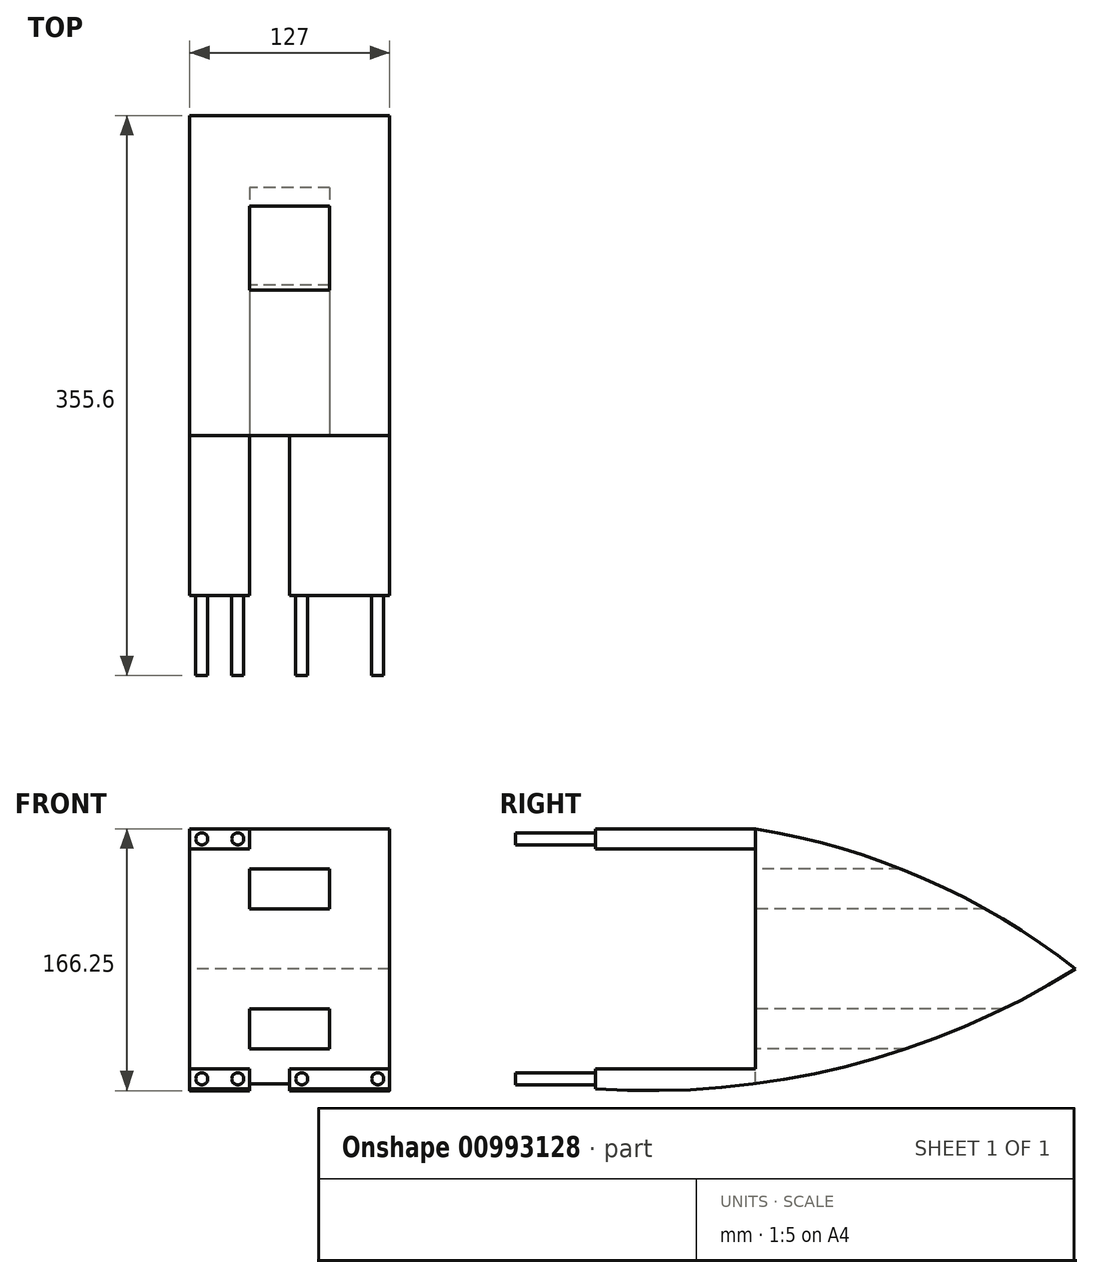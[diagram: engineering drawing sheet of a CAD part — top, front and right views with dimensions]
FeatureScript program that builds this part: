
annotation { "Feature Type Name" : "Feature", "Feature Type Description" : "" }
export const myFeature = defineFeature(function(context is Context, id is Id, definition is map)
    precondition{}
    {
        {
            var Q0;
            Q0=qCreatedBy(makeId("Right.planeOp"),FACE);
            var sketch = newSketch(context, id + "F0", { "sketchPlane" : qUnion([Q0])});
            skLineSegment(sketch, "E0", {"start": v(-50.03, 29.01) * mm, "end": v(153.17, 29.01) * mm});
            skLineSegment(sketch, "E1", {"start": v(-50.03, 29.01) * mm, "end": v(-50.03, 117.91) * mm});
            skLineSegment(sketch, "E2", {"start": v(-50.03, 29.01) * mm, "end": v(-50.03, -34.49) * mm});
            skLineSegment(sketch, "E3", {"start": v(-50.03, -34.49) * mm, "end": v(-151.63, -34.49) * mm});
            skLineSegment(sketch, "E4", {"start": v(-151.63, -34.49) * mm, "end": v(-151.63, -47.19) * mm});
            skArc(sketch, "E5", {"start": v(-151.63, -47.19) * mm, "mid": v(6.77, -33.08) * mm, "end": v(153.17, 29.01) * mm});
            skArc(sketch, "E6", {"start": v(153.17, 29.01) * mm, "mid": v(57.18, 86.27) * mm, "end": v(-50.03, 117.91) * mm});
            skSolve(sketch);
        }
        {
            var Q0;
            Q0=makeQuery(id+"F0.imprint","IMPRINT",FACE,{"disambiguationData":[TD([[makeQuery(id+"F0.imprint","IMPRINT",EDGE,{"derivedFrom":sQuery(id+"F0.wireOp",EDGE,"E0")}),1.0]])]});
            var Q1;
            Q1=makeQuery(id+"F0.imprint","IMPRINT",FACE,{"disambiguationData":[TD([[makeQuery(id+"F0.imprint","IMPRINT",EDGE,{"derivedFrom":sQuery(id+"F0.wireOp",EDGE,"E0")}),-1.0]])]});
            extrude(context, id + "F1", {"entities" : qUnion([Q0, Q1]), "depth" : 127 * mm, "offsetDistance" : 25.4 * mm});
        }
        {
            var Q0;
            Q0=makeQuery(id+"F1.opExtrude","SWEPT_FACE",FACE,{"disambiguationData":[OSD([sQuery(id+"F0.wireOp",EDGE,"E3")])]});
            var sketch = newSketch(context, id + "F2", { "sketchPlane" : qUnion([Q0])});
            skLineSegment(sketch, "E7.bottom", {"start": v(63.5, -50.03) * mm, "end": v(38.1, -50.03) * mm});
            skLineSegment(sketch, "E7.top", {"start": v(63.5, -151.63) * mm, "end": v(38.1, -151.63) * mm});
            skLineSegment(sketch, "E7.left", {"start": v(63.5, -50.03) * mm, "end": v(63.5, -151.63) * mm});
            skLineSegment(sketch, "E7.right", {"start": v(38.1, -50.03) * mm, "end": v(38.1, -151.63) * mm});
            skSolve(sketch);
        }
        {
            var Q0;
            Q0=makeQuery(id+"F2.imprint","IMPRINT",FACE,{"disambiguationData":[TD([[makeQuery(id+"F2.imprint","IMPRINT",EDGE,{"derivedFrom":sQuery(id+"F2.wireOp",EDGE,"E7.bottom")}),1.0]])]});
            extrude(context, id + "F3", {"entities" : qUnion([Q0]), "operationType" : NewBodyOperationType.REMOVE, "oppositeDirection" : true, "depth" : 25.4 * mm, "offsetDistance" : 25.4 * mm});
        }
        {
            var Q0;
            Q0=makeQuery(id+"F3.boolean.opBoolean","MERGE",FACE,{"derivedFrom":[makeQuery(id+"F1.opExtrude","SWEPT_FACE",FACE,{"disambiguationData":[OSD([sQuery(id+"F0.wireOp",EDGE,"E1"),sQuery(id+"F0.wireOp",EDGE,"E2")])]})],"fromTools":[makeQuery(id+"F3.opExtrude","SWEPT_FACE",FACE,{"disambiguationData":[OSD([sQuery(id+"F2.wireOp",EDGE,"E7.bottom")])]})]});
            var sketch = newSketch(context, id + "F4", { "sketchPlane" : qUnion([Q0])});
            skLineSegment(sketch, "E8.bottom", {"start": v(88.9, 92.51) * mm, "end": v(38.1, 92.51) * mm});
            skLineSegment(sketch, "E8.top", {"start": v(88.9, 67.11) * mm, "end": v(38.1, 67.11) * mm});
            skLineSegment(sketch, "E8.left", {"start": v(88.9, 92.51) * mm, "end": v(88.9, 67.11) * mm});
            skLineSegment(sketch, "E8.right", {"start": v(38.1, 92.51) * mm, "end": v(38.1, 67.11) * mm});
            skPoint(sketch, "E8.middle", {"position": v(63.5, 79.81) * mm});
            skPoint(sketch, "E8.middle.positionSnap0", {"position": v(63.5, 117.91) * mm});
            skPoint(sketch, "E8.centerSnap0", {"position": v(63.5, 117.91) * mm});
            skLineSegment(sketch, "E9.bottom", {"start": v(88.9, 3.61) * mm, "end": v(38.1, 3.61) * mm});
            skLineSegment(sketch, "E9.top", {"start": v(88.9, -21.79) * mm, "end": v(38.1, -21.79) * mm});
            skLineSegment(sketch, "E9.left", {"start": v(88.9, 3.61) * mm, "end": v(88.9, -21.79) * mm});
            skLineSegment(sketch, "E9.right", {"start": v(38.1, 3.61) * mm, "end": v(38.1, -21.79) * mm});
            skPoint(sketch, "E9.middle", {"position": v(63.5, -9.09) * mm});
            skSolve(sketch);
        }
        {
            var Q0;
            Q0=makeQuery(id+"F4.imprint","IMPRINT",FACE,{"disambiguationData":[TD([[makeQuery(id+"F4.imprint","IMPRINT",EDGE,{"derivedFrom":sQuery(id+"F4.wireOp",EDGE,"E8.bottom")}),1.0]])]});
            var Q1;
            Q1=makeQuery(id+"F4.imprint","IMPRINT",FACE,{"disambiguationData":[TD([[makeQuery(id+"F4.imprint","IMPRINT",EDGE,{"derivedFrom":sQuery(id+"F4.wireOp",EDGE,"E9.bottom")}),1.0]])]});
            extrude(context, id + "F5", {"entities" : qUnion([Q0, Q1]), "operationType" : NewBodyOperationType.REMOVE, "oppositeDirection" : true, "depth" : 203.2 * mm, "offsetDistance" : 25.4 * mm});
        }
        {
            var Q0;
            {var subQ1=sQuery(id+"F0.wireOp",EDGE,"E4");Q0=makeQuery(id+"F3.boolean.opBoolean","SPLIT",FACE,{"disambiguationData":[TD([makeQuery(id+"F3.opExtrude","SWEPT_FACE",FACE,{"disambiguationData":[OSD([sQuery(id+"F2.wireOp",EDGE,"E7.left")])]})])],"derivedFrom":makeQuery(id+"F1.opExtrude","SWEPT_FACE",FACE,{"disambiguationData":[OSD([subQ1])]})});}
            var sketch = newSketch(context, id + "F6", { "sketchPlane" : qUnion([Q0])});
            skCircle(sketch, "E10", {"center": v(119.38, -40.84) * mm, "radius": 3.81 * mm});
            skPoint(sketch, "E10.centerSnap0", {"position": v(127, -40.84) * mm});
            skCircle(sketch, "E11", {"center": v(71.12, -40.84) * mm, "radius": 3.81 * mm});
            skPoint(sketch, "E11.centerSnap0", {"position": v(63.5, -40.84) * mm});
            skSolve(sketch);
        }
        {
            var Q0;
            Q0=makeQuery(id+"F6.imprint","IMPRINT",FACE,{"disambiguationData":[TD([[makeQuery(id+"F6.imprint","IMPRINT",EDGE,{"derivedFrom":sQuery(id+"F6.wireOp",EDGE,"E11")}),1.0]])]});
            var Q1;
            Q1=makeQuery(id+"F6.imprint","IMPRINT",FACE,{"disambiguationData":[TD([[makeQuery(id+"F6.imprint","IMPRINT",EDGE,{"derivedFrom":sQuery(id+"F6.wireOp",EDGE,"E10")}),1.0]])]});
            extrude(context, id + "F7", {"entities" : qUnion([Q0, Q1]), "operationType" : NewBodyOperationType.ADD, "depth" : 50.8 * mm, "offsetDistance" : 25.4 * mm});
        }
        {
            var Q0;
            {var subQ1=sQuery(id+"F0.wireOp",EDGE,"E4");Q0=makeQuery(id+"F3.boolean.opBoolean","SPLIT",FACE,{"disambiguationData":[TD([makeQuery(id+"F3.opExtrude","SWEPT_FACE",FACE,{"disambiguationData":[OSD([sQuery(id+"F2.wireOp",EDGE,"E7.right")])]})])],"derivedFrom":makeQuery(id+"F1.opExtrude","SWEPT_FACE",FACE,{"disambiguationData":[OSD([subQ1])]})});}
            var sketch = newSketch(context, id + "F8", { "sketchPlane" : qUnion([Q0])});
            skCircle(sketch, "E12", {"center": v(30.48, -40.84) * mm, "radius": 3.81 * mm});
            skPoint(sketch, "E12.centerSnap0", {"position": v(38.1, -40.84) * mm});
            skCircle(sketch, "E13", {"center": v(7.62, -40.84) * mm, "radius": 3.82 * mm});
            skPoint(sketch, "E13.centerSnap0", {"position": v(0, -40.84) * mm});
            skSolve(sketch);
        }
        {
            var Q0;
            Q0=makeQuery(id+"F8.imprint","IMPRINT",FACE,{"disambiguationData":[TD([[makeQuery(id+"F8.imprint","IMPRINT",EDGE,{"derivedFrom":sQuery(id+"F8.wireOp",EDGE,"E13")}),1.0]])]});
            var Q1;
            Q1=makeQuery(id+"F8.imprint","IMPRINT",FACE,{"disambiguationData":[TD([[makeQuery(id+"F8.imprint","IMPRINT",EDGE,{"derivedFrom":sQuery(id+"F8.wireOp",EDGE,"E12")}),1.0]])]});
            extrude(context, id + "F9", {"entities" : qUnion([Q0, Q1]), "operationType" : NewBodyOperationType.ADD, "depth" : 50.8 * mm, "offsetDistance" : 25.4 * mm});
        }
        {
            var Q0;
            Q0=makeQuery(id+"F3.boolean.opBoolean","MERGE",FACE,{"derivedFrom":[makeQuery(id+"F1.opExtrude","SWEPT_FACE",FACE,{"disambiguationData":[OSD([sQuery(id+"F0.wireOp",EDGE,"E1"),sQuery(id+"F0.wireOp",EDGE,"E2")])]})],"fromTools":[makeQuery(id+"F3.opExtrude","SWEPT_FACE",FACE,{"disambiguationData":[OSD([sQuery(id+"F2.wireOp",EDGE,"E7.bottom")])]})]});
            var sketch = newSketch(context, id + "F10", { "sketchPlane" : qUnion([Q0])});
            skLineSegment(sketch, "E14.bottom", {"start": v(38.1, 105.21) * mm, "end": v(0, 105.21) * mm});
            skLineSegment(sketch, "E14.top", {"start": v(38.1, 117.91) * mm, "end": v(0, 117.91) * mm});
            skLineSegment(sketch, "E14.left", {"start": v(38.1, 105.21) * mm, "end": v(38.1, 117.91) * mm});
            skLineSegment(sketch, "E14.right", {"start": v(0, 105.21) * mm, "end": v(0, 117.91) * mm});
            skSolve(sketch);
        }
        {
            var Q0;
            Q0=makeQuery(id+"F10.imprint","IMPRINT",FACE,{"disambiguationData":[TD([[makeQuery(id+"F10.imprint","IMPRINT",EDGE,{"derivedFrom":sQuery(id+"F10.wireOp",EDGE,"E14.bottom")}),-1.0]])]});
            extrude(context, id + "F11", {"entities" : qUnion([Q0]), "operationType" : NewBodyOperationType.ADD, "depth" : 101.6 * mm, "offsetDistance" : 25.4 * mm});
        }
        {
            var Q0;
            Q0=makeQuery(id+"F11.opExtrude","CAP_FACE",FACE,{"disambiguationData":[OSD([sQuery(id+"F10.wireOp",EDGE,"E14.bottom"),sQuery(id+"F10.wireOp",EDGE,"E14.top"),sQuery(id+"F10.wireOp",EDGE,"E14.left"),sQuery(id+"F10.wireOp",EDGE,"E14.right")])],"isStart":false});
            var sketch = newSketch(context, id + "F12", { "sketchPlane" : qUnion([Q0])});
            skCircle(sketch, "E15", {"center": v(30.48, 111.56) * mm, "radius": 3.81 * mm});
            skPoint(sketch, "E15.centerSnap0", {"position": v(38.1, 111.56) * mm});
            skCircle(sketch, "E16", {"center": v(7.62, 111.56) * mm, "radius": 3.81 * mm});
            skPoint(sketch, "E16.centerSnap0", {"position": v(0, 111.56) * mm});
            skSolve(sketch);
        }
        {
            var Q0;
            Q0=makeQuery(id+"F12.imprint","IMPRINT",FACE,{"disambiguationData":[TD([[makeQuery(id+"F12.imprint","IMPRINT",EDGE,{"derivedFrom":sQuery(id+"F12.wireOp",EDGE,"E15")}),1.0]])]});
            var Q1;
            Q1=makeQuery(id+"F12.imprint","IMPRINT",FACE,{"disambiguationData":[TD([[makeQuery(id+"F12.imprint","IMPRINT",EDGE,{"derivedFrom":sQuery(id+"F12.wireOp",EDGE,"E16")}),1.0]])]});
            extrude(context, id + "F13", {"entities" : qUnion([Q0, Q1]), "operationType" : NewBodyOperationType.ADD, "depth" : 50.8 * mm, "offsetDistance" : 25.4 * mm});
        }
    });
